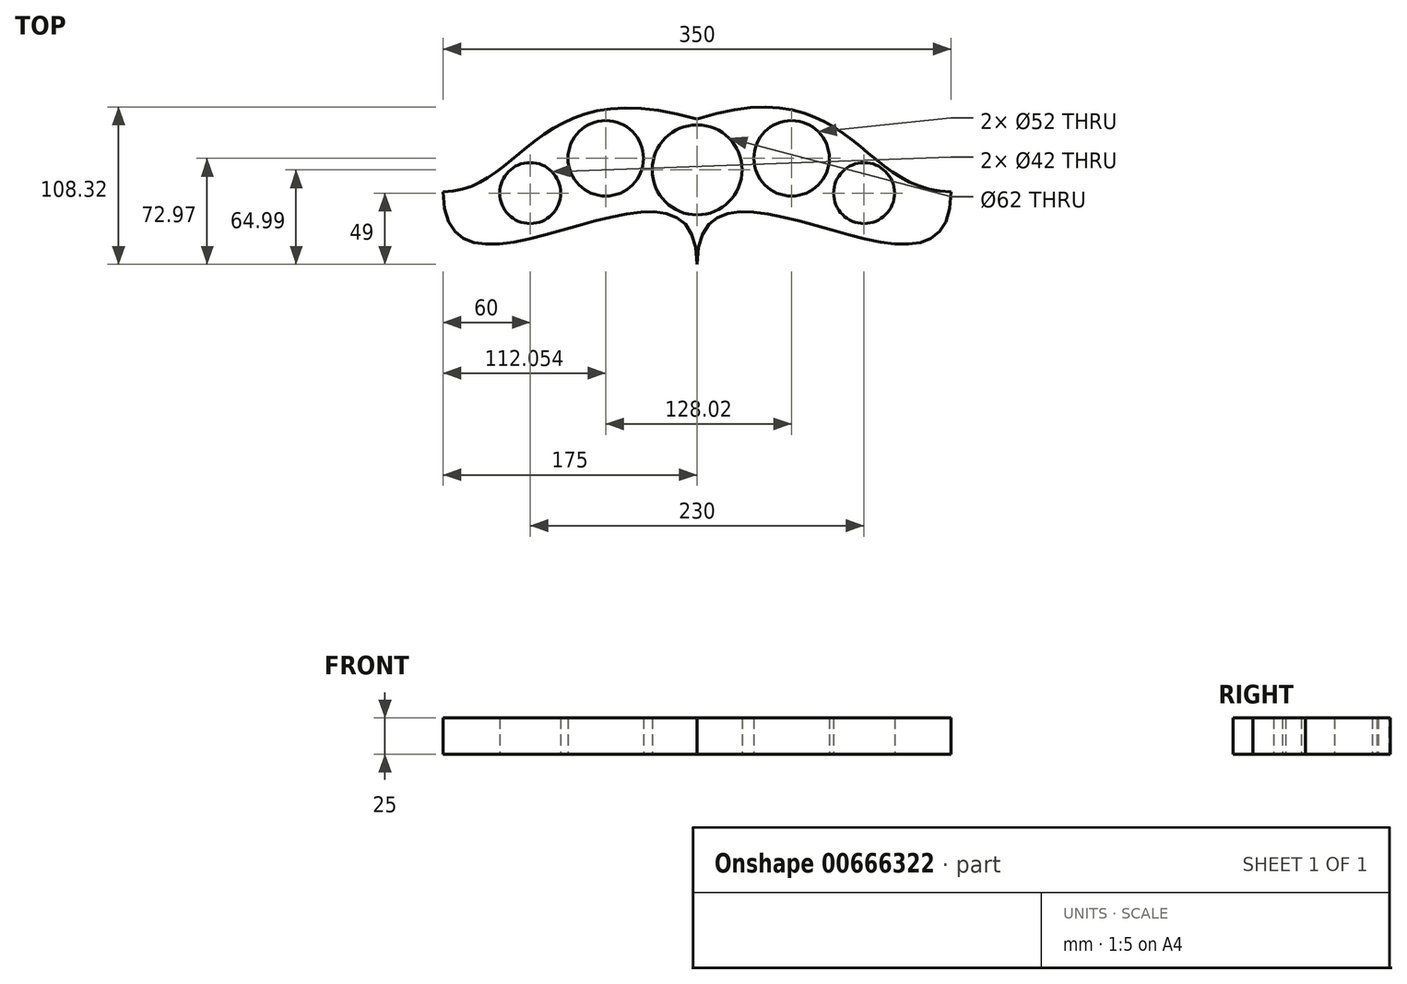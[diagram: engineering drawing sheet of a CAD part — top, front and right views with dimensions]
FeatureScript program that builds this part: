
annotation { "Feature Type Name" : "Feature", "Feature Type Description" : "" }
export const myFeature = defineFeature(function(context is Context, id is Id, definition is map)
    precondition{}
    {
        {
            var Q0;
            Q0=qCreatedBy(makeId("Top.planeOp"),FACE);
            var sketch = newSketch(context, id + "F0", { "sketchPlane" : qUnion([Q0])});
            skPoint(sketch, "E0", {"position": v(-175, 0) * mm});
            skPoint(sketch, "E1", {"position": v(175, 0) * mm});
            skPoint(sketch, "E2", {"position": v(0, -50) * mm});
            skPoint(sketch, "E3", {"position": v(0, 50) * mm});
            skFitSpline(sketch, "E4", {"points": [v(-175, 0) * mm, v(0, 50) * mm], "startDerivative": vector(166.13, 0) * mm, "endDerivative": vector(334.8, -98.44) * mm});
            skFitSpline(sketch, "E5", {"points": [v(0, 50) * mm, v(175, 0) * mm], "startDerivative": vector(319.13, 103.91) * mm, "endDerivative": vector(189.47, 0) * mm});
            skFitSpline(sketch, "E6", {"points": [v(175, 0) * mm, v(0, -50) * mm], "startDerivative": vector(0, -300) * mm, "endDerivative": vector(0, -300) * mm});
            skFitSpline(sketch, "E7", {"points": [v(-175, 0) * mm, v(0, -50) * mm], "startDerivative": vector(0, -300) * mm, "endDerivative": vector(0, -300) * mm});
            skPoint(sketch, "E8", {"position": v(0, -100) * mm});
            skPoint(sketch, "E9", {"position": v(-115, -1) * mm});
            skPoint(sketch, "E10", {"position": v(115, -1) * mm});
            skPoint(sketch, "E11", {"position": v(0, 15) * mm});
            skCircle(sketch, "E12", {"center": v(0, 15) * mm, "radius": 31 * mm});
            skCircle(sketch, "E13", {"center": v(-115, -1) * mm, "radius": 21 * mm});
            skCircle(sketch, "E14", {"center": v(115, -1) * mm, "radius": 21 * mm});
            skPoint(sketch, "E15", {"position": v(-62.95, 22.98) * mm});
            skPoint(sketch, "E16", {"position": v(65.07, 22.98) * mm});
            skCircle(sketch, "E17", {"center": v(-62.95, 22.98) * mm, "radius": 26 * mm});
            skCircle(sketch, "E18", {"center": v(65.07, 22.98) * mm, "radius": 26 * mm});
            skSolve(sketch);
        }
        {
            var Q0;
            Q0 = qSketchRegion(id + "F0", true);
            extrude(context, id + "F1", {"entities" : qUnion([Q0]), "depth" : 25 * mm, "offsetDistance" : 25 * mm});
        }
    });
